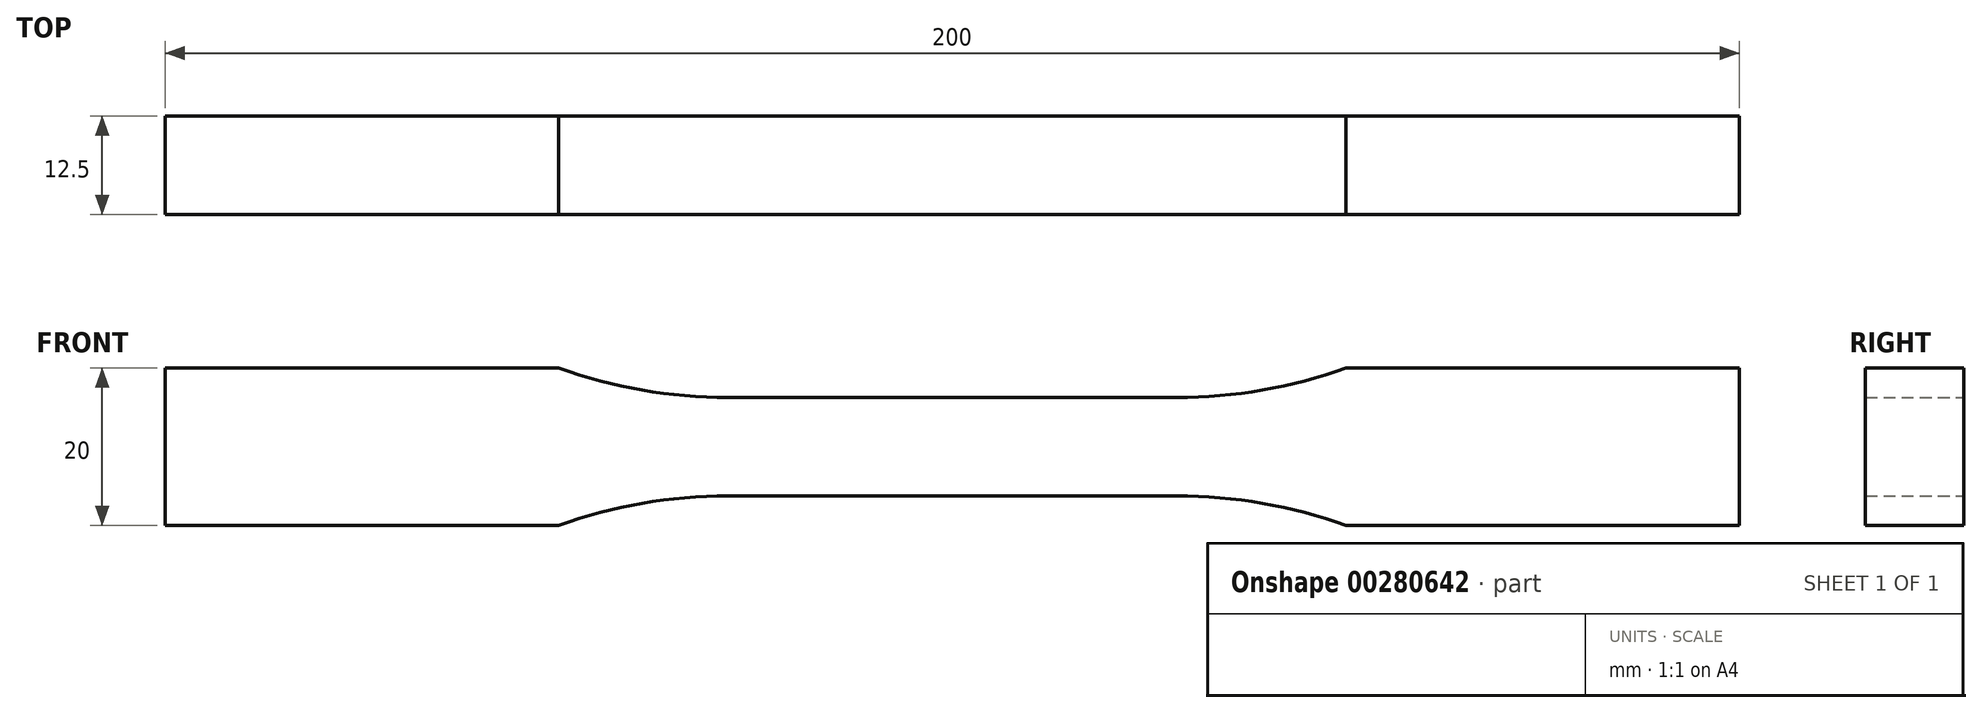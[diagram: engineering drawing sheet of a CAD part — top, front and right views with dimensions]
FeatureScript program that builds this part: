
annotation { "Feature Type Name" : "Feature", "Feature Type Description" : "" }
export const myFeature = defineFeature(function(context is Context, id is Id, definition is map)
    precondition{}
    {
        {
            var Q0;
            Q0=qCreatedBy(makeId("Front.planeOp"),FACE);
            var sketch = newSketch(context, id + "F0", { "sketchPlane" : qUnion([Q0])});
            skLineSegment(sketch, "E0", {"start": v(0, 6.25) * mm, "end": v(28.5, 6.25) * mm});
            skArc(sketch, "E1", {"start": v(28.5, 6.25) * mm, "mid": v(39.41, 7.2) * mm, "end": v(50, 10) * mm});
            skLineSegment(sketch, "E2", {"start": v(50, 10) * mm, "end": v(100, 10) * mm});
            skLineSegment(sketch, "E3", {"start": v(100, 10) * mm, "end": v(100, 0) * mm});
            skLineSegment(sketch, "E4.MirrorCS", {"start": v(0, -6.25) * mm, "end": v(28.5, -6.25) * mm});
            skArc(sketch, "E5.MirrorCS", {"start": v(28.5, -6.25) * mm, "mid": v(39.41, -7.2) * mm, "end": v(50, -10) * mm});
            skLineSegment(sketch, "E6.MirrorCS", {"start": v(50, -10) * mm, "end": v(100, -10) * mm});
            skLineSegment(sketch, "E7.MirrorCS", {"start": v(100, -10) * mm, "end": v(100, 0) * mm});
            skLineSegment(sketch, "E8.MirrorCS", {"start": v(0, 6.25) * mm, "end": v(-28.5, 6.25) * mm});
            skArc(sketch, "E9.MirrorCS", {"start": v(-28.5, 6.25) * mm, "mid": v(-39.41, 7.2) * mm, "end": v(-50, 10) * mm});
            skLineSegment(sketch, "E10.MirrorCS", {"start": v(-50, 10) * mm, "end": v(-100, 10) * mm});
            skLineSegment(sketch, "E11.MirrorCS", {"start": v(-100, 10) * mm, "end": v(-100, 0) * mm});
            skLineSegment(sketch, "E12.MirrorCS", {"start": v(-100, -10) * mm, "end": v(-100, 0) * mm});
            skLineSegment(sketch, "E13.MirrorCS", {"start": v(-50, -10) * mm, "end": v(-100, -10) * mm});
            skArc(sketch, "E14.MirrorCS", {"start": v(-28.5, -6.25) * mm, "mid": v(-39.41, -7.2) * mm, "end": v(-50, -10) * mm});
            skLineSegment(sketch, "E15.MirrorCS", {"start": v(0, -6.25) * mm, "end": v(-28.5, -6.25) * mm});
            skSolve(sketch);
        }
        {
            var Q0;
            Q0 = qSketchRegion(id + "F0", true);
            extrude(context, id + "F1", {"entities" : qUnion([Q0]), "endBound" : BoundingType.SYMMETRIC, "depth" : 12.5 * mm});
        }
    });
